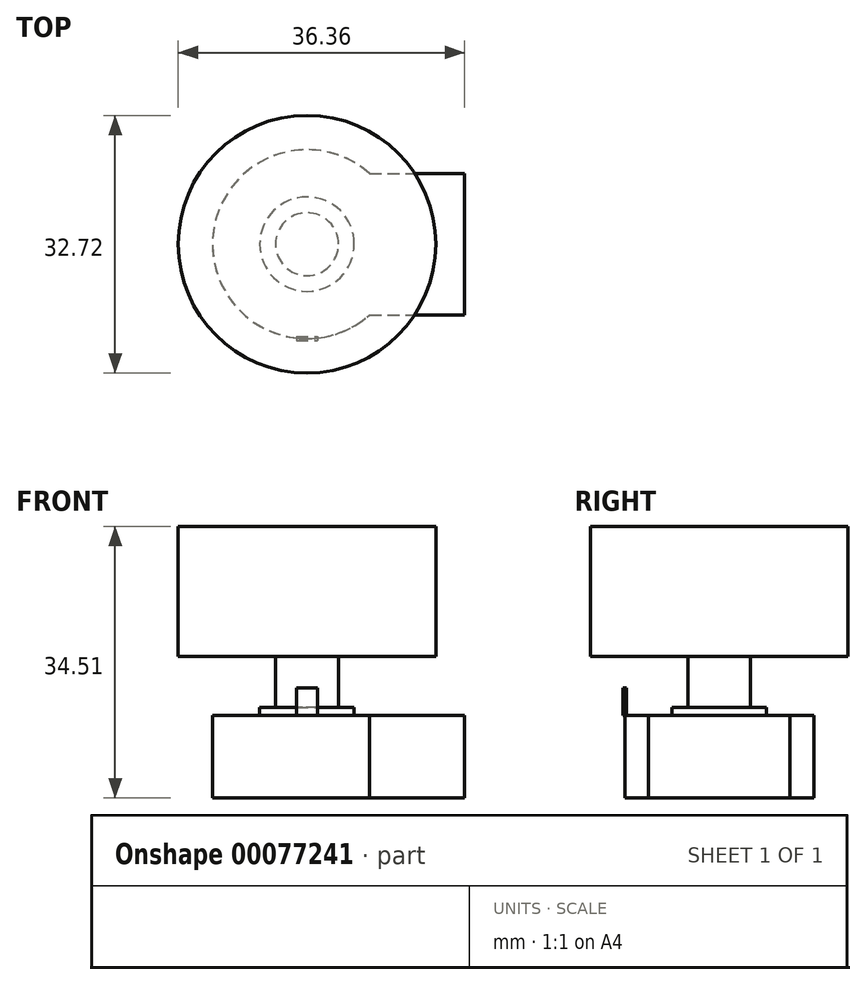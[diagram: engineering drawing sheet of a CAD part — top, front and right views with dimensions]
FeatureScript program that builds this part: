
annotation { "Feature Type Name" : "Feature", "Feature Type Description" : "" }
export const myFeature = defineFeature(function(context is Context, id is Id, definition is map)
    precondition{}
    {
        {
            var Q0;
            Q0=qCreatedBy(makeId("Top.planeOp"),FACE);
            var sketch = newSketch(context, id + "F0", { "sketchPlane" : qUnion([Q0])});
            skCircle(sketch, "E0", {"center": v(0, 0) * mm, "radius": 6 * mm});
            skSolve(sketch);
        }
        {
            var Q0;
            Q0 = qSketchRegion(id + "F0", true);
            extrude(context, id + "F1", {"entities" : qUnion([Q0]), "oppositeDirection" : true, "depth" : 1 * mm});
        }
        {
            var Q0;
            Q0=makeQuery(id+"F1.opExtrude","CAP_FACE",FACE,{"disambiguationData":[OSD([sQuery(id+"F0.wireOp",EDGE,"E0")])],"isStart":false});
            var sketch = newSketch(context, id + "F2", { "sketchPlane" : qUnion([Q0])});
            skCircle(sketch, "E1", {"center": v(0, 0) * mm, "radius": 12 * mm});
            skSolve(sketch);
        }
        {
            var Q0;
            Q0=makeQuery(id+"F2.imprint","IMPRINT",FACE,{"disambiguationData":[TD([[makeQuery(id+"F2.imprint","IMPRINT",EDGE,{"derivedFrom":sQuery(id+"F2.wireOp",EDGE,"E1")}),1.0]])]});
            var Q1;
            Q1=makeQuery(id+"F2.imprint","IMPRINT",FACE,{"disambiguationData":[TD([[makeQuery(id+"F2.imprint","IMPRINT",EDGE,{"derivedFrom":makeQuery(id+"F1.opExtrude","CAP_EDGE",EDGE,{"disambiguationData":[OSD([sQuery(id+"F0.wireOp",EDGE,"E0")])],"isStart":false})}),-1.0]])]});
            extrude(context, id + "F3", {"entities" : qUnion([Q0, Q1]), "operationType" : NewBodyOperationType.ADD, "depth" : 10.5 * mm});
        }
        {
            var Q0;
            Q0=makeQuery(id+"F3.opExtrude","CAP_FACE",FACE,{"disambiguationData":[OSD([sQuery(id+"F2.wireOp",EDGE,"E1")])],"isStart":true});
            var sketch = newSketch(context, id + "F4", { "sketchPlane" : qUnion([Q0])});
            skLineSegment(sketch, "E2.bottom", {"start": v(6.35, -9) * mm, "end": v(20, -9) * mm});
            skLineSegment(sketch, "E2.top", {"start": v(6.35, 9) * mm, "end": v(20, 9) * mm});
            skLineSegment(sketch, "E2.left", {"start": v(6.35, -9) * mm, "end": v(6.35, 9) * mm});
            skLineSegment(sketch, "E2.right", {"start": v(20, -9) * mm, "end": v(20, 9) * mm});
            skLineSegment(sketch, "E3", {"start": v(0, 0) * mm, "end": v(6.35, 0) * mm, "construction": true});
            skSolve(sketch);
        }
        {
            var Q0;
            Q0=makeQuery(id+"F4.imprint","IMPRINT",FACE,{"disambiguationData":[TD([[makeQuery(id+"F4.imprint","IMPRINT",EDGE,{"derivedFrom":sQuery(id+"F4.wireOp",EDGE,"E2.bottom")}),1.0]])]});
            var Q1;
            Q1=makeQuery(id+"F3.opExtrude","CAP_FACE",FACE,{"disambiguationData":[OSD([sQuery(id+"F2.wireOp",EDGE,"E1")])],"isStart":false});
            extrude(context, id + "F5", {"entities" : qUnion([Q0]), "operationType" : NewBodyOperationType.ADD, "endBound" : BoundingType.UP_TO_SURFACE, "oppositeDirection" : true, "endBoundEntityFace" : qUnion([Q1]), "depth" : 25.4 * mm});
        }
        {
            var Q0;
            Q0=makeQuery(id+"F1.opExtrude","CAP_FACE",FACE,{"disambiguationData":[OSD([sQuery(id+"F0.wireOp",EDGE,"E0")])],"isStart":true});
            var sketch = newSketch(context, id + "F6", { "sketchPlane" : qUnion([Q0])});
            skCircle(sketch, "E4", {"center": v(0, 0) * mm, "radius": 4 * mm});
            skSolve(sketch);
        }
        {
            var Q0;
            Q0 = qSketchRegion(id + "F6", true);
            extrude(context, id + "F7", {"entities" : qUnion([Q0]), "operationType" : NewBodyOperationType.ADD, "depth" : 6.5 * mm});
        }
        {
            var Q0;
            Q0=makeQuery(id+"F7.opExtrude","CAP_FACE",FACE,{"disambiguationData":[OSD([sQuery(id+"F6.wireOp",EDGE,"E4")])],"isStart":false});
            var sketch = newSketch(context, id + "F8", { "sketchPlane" : qUnion([Q0])});
            skCircle(sketch, "E5", {"center": v(0, 0) * mm, "radius": 3 * mm});
            skSolve(sketch);
        }
        {
            var Q0;
            Q0 = qSketchRegion(id + "F8", true);
            extrude(context, id + "F9", {"entities" : qUnion([Q0]), "operationType" : NewBodyOperationType.ADD, "depth" : 8.38 * mm});
        }
        {
            var Q0;
            Q0=makeQuery(id+"F5.boolean.opBoolean","MERGE",FACE,{"derivedFrom":[makeQuery(id+"F3.opExtrude","CAP_FACE",FACE,{"disambiguationData":[OSD([sQuery(id+"F2.wireOp",EDGE,"E1")])],"isStart":true}),makeQuery(id+"F5.opExtrude","CAP_FACE",FACE,{"disambiguationData":[OSD([sQuery(id+"F4.wireOp",EDGE,"E2.bottom"),sQuery(id+"F4.wireOp",EDGE,"E2.top"),sQuery(id+"F4.wireOp",EDGE,"E2.left"),sQuery(id+"F4.wireOp",EDGE,"E2.right")])],"isStart":true})]});
            var sketch = newSketch(context, id + "F10", { "sketchPlane" : qUnion([Q0])});
            skLineSegment(sketch, "E6.bottom", {"start": v(-1.35, -11.75) * mm, "end": v(1.35, -11.75) * mm});
            skLineSegment(sketch, "E6.top", {"start": v(-1.35, -12.25) * mm, "end": v(1.35, -12.25) * mm});
            skLineSegment(sketch, "E6.left", {"start": v(-1.35, -11.75) * mm, "end": v(-1.35, -12.25) * mm});
            skLineSegment(sketch, "E6.right", {"start": v(1.35, -11.75) * mm, "end": v(1.35, -12.25) * mm});
            skLineSegment(sketch, "E7", {"start": v(-1.35, -12) * mm, "end": v(1.35, -12) * mm, "construction": true});
            skLineSegment(sketch, "E8", {"start": v(0, -11.75) * mm, "end": v(0, 0) * mm, "construction": true});
            skSolve(sketch);
        }
        {
            var Q0;
            Q0 = qSketchRegion(id + "F10", true);
            extrude(context, id + "F11", {"entities" : qUnion([Q0]), "operationType" : NewBodyOperationType.ADD, "depth" : 3.5 * mm});
        }
        {
            var Q0;
            Q0=makeQuery(id+"F7.opExtrude","CAP_FACE",FACE,{"disambiguationData":[OSD([sQuery(id+"F6.wireOp",EDGE,"E4")])],"isStart":false});
            var sketch = newSketch(context, id + "F12", { "sketchPlane" : qUnion([Q0])});
            skCircle(sketch, "E9", {"center": v(0, 0) * mm, "radius": 16.36 * mm});
            skSolve(sketch);
        }
        {
            var Q0;
            Q0 = qSketchRegion(id + "F12", true);
            extrude(context, id + "F13", {"entities" : qUnion([Q0]), "operationType" : NewBodyOperationType.ADD, "depth" : 16.5 * mm});
        }
    });
